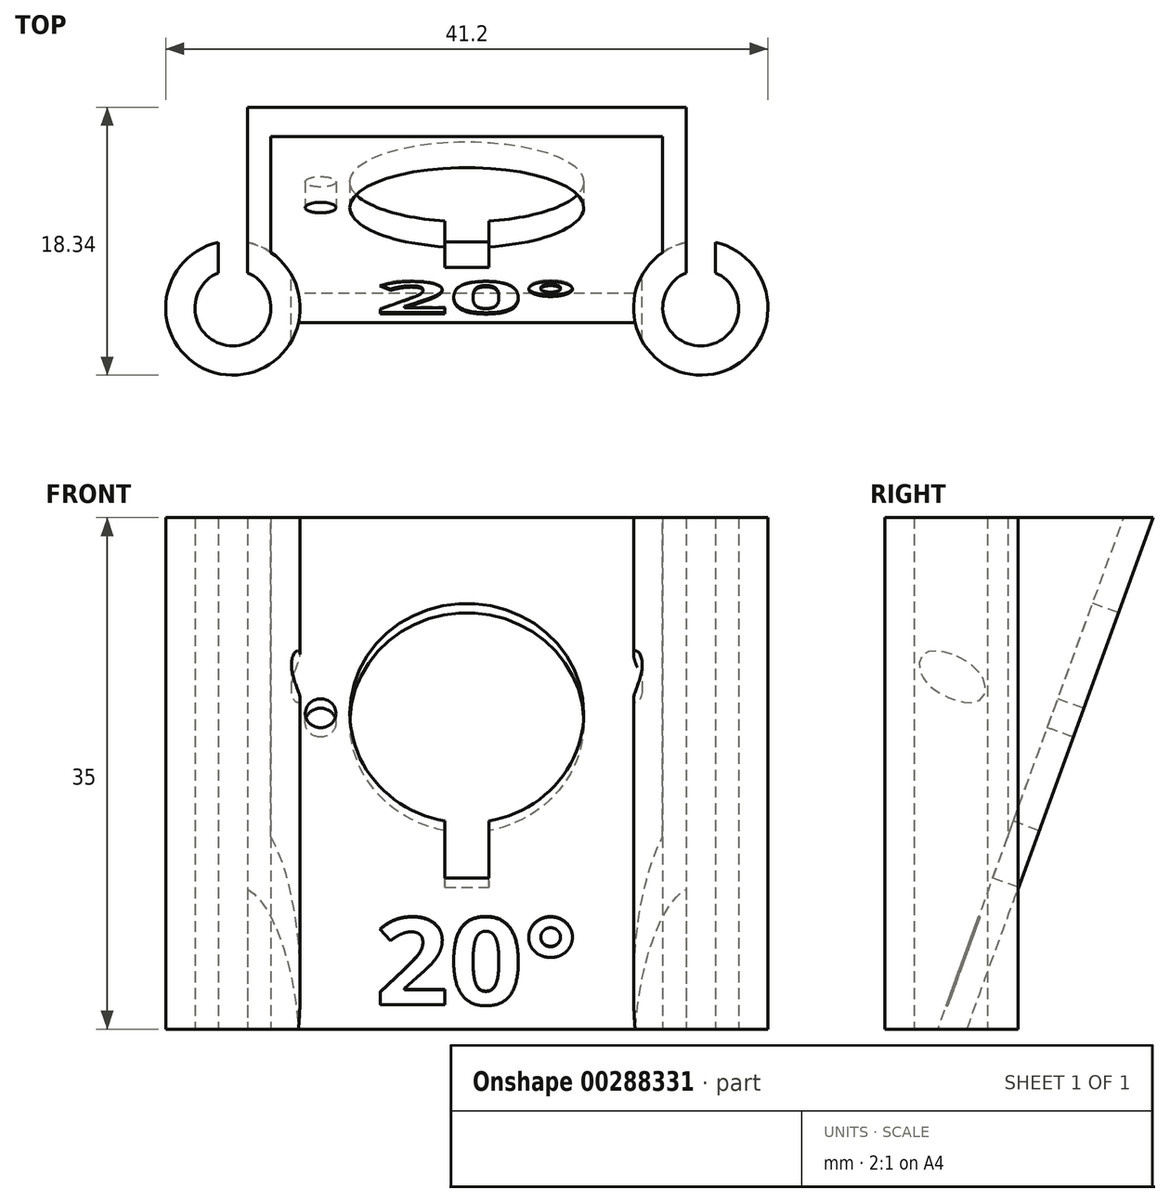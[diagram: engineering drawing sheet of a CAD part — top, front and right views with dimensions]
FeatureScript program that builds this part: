
annotation { "Feature Type Name" : "Feature", "Feature Type Description" : "" }
export const myFeature = defineFeature(function(context is Context, id is Id, definition is map)
    precondition{}
    {
        {
            var Q0;
            Q0=qCreatedBy(makeId("Top.planeOp"),FACE);
            var sketch = newSketch(context, id + "F0", { "sketchPlane" : qUnion([Q0])});
            skLineSegment(sketch, "E0", {"start": v(0, 0) * mm, "end": v(-16, 0) * mm, "construction": true});
            skCircle(sketch, "E1", {"center": v(-16, 0) * mm, "radius": 2.6 * mm});
            skCircle(sketch, "E2.0", {"center": v(-16, 0) * mm, "radius": 4.6 * mm});
            skSolve(sketch);
        }
        {
            var Q0;
            Q0 = qSketchRegion(id + "F0", true);
            extrude(context, id + "F1", {"entities" : qUnion([Q0]), "depth" : 35 * mm});
        }
        {
            var Q0;
            Q0=qCreatedBy(makeId("Top.planeOp"),FACE);
            var sketch = newSketch(context, id + "F2", { "sketchPlane" : qUnion([Q0])});
            skCircle(sketch, "E3.0", {"center": v(-16, 0) * mm, "radius": 2.6 * mm, "construction": true});
            skLineSegment(sketch, "E4", {"start": v(-16, 0) * mm, "end": v(-16, 2.6) * mm, "construction": true});
            skLineSegment(sketch, "E5.bottom", {"start": v(-15, 5.66) * mm, "end": v(-17, 5.66) * mm});
            skLineSegment(sketch, "E5.top", {"start": v(-15, -0.46) * mm, "end": v(-17, -0.46) * mm});
            skLineSegment(sketch, "E5.left", {"start": v(-15, 5.66) * mm, "end": v(-15, -0.46) * mm});
            skLineSegment(sketch, "E5.right", {"start": v(-17, 5.66) * mm, "end": v(-17, -0.46) * mm});
            skPoint(sketch, "E5.middle", {"position": v(-16, 2.6) * mm});
            skSolve(sketch);
        }
        {
            var Q0;
            Q0 = qSketchRegion(id + "F2", true);
            extrude(context, id + "F3", {"entities" : qUnion([Q0]), "operationType" : NewBodyOperationType.REMOVE, "endBound" : BoundingType.THROUGH_ALL, "depth" : 25 * mm});
        }
        {
            var Q0;
            Q0=qCreatedBy(makeId("Top.planeOp"),FACE);
            cPlane(context, id + "F4", {"entities" : qUnion([Q0]), "cplaneType" : CPlaneType.OFFSET, "offset" : 35 * mm, "width" : 150 * mm, "height" : 150 * mm});
        }
        {
            var Q0;
            Q0=makeQuery(id+"F1.opExtrude","SWEPT_BODY",BODY,{"disambiguationData":[OSD([sQuery(id+"F0.wireOp",EDGE,"E1"),sQuery(id+"F0.wireOp",EDGE,"E2.0")])]});
            var Q1;
            Q1=qCreatedBy(makeId("Right.planeOp"),FACE);
            mirror(context, id + "F5", {"entities" : qUnion([Q0]), "mirrorPlane" : qUnion([Q1])});
        }
        {
            var Q0;
            Q0=qCreatedBy(makeId("Top.planeOp"),FACE);
            var sketch = newSketch(context, id + "F6", { "sketchPlane" : qUnion([Q0])});
            skLineSegment(sketch, "E6.bottom", {"start": v(13.4, -1) * mm, "end": v(-13.4, -1) * mm});
            skLineSegment(sketch, "E6.top", {"start": v(13.4, 1) * mm, "end": v(-13.4, 1) * mm});
            skLineSegment(sketch, "E6.left", {"start": v(13.4, -1) * mm, "end": v(13.4, 1) * mm});
            skLineSegment(sketch, "E6.right", {"start": v(-13.4, -1) * mm, "end": v(-13.4, 1) * mm});
            skPoint(sketch, "E6.middle", {"position": v(0, 0) * mm});
            skSolve(sketch);
        }
        {
            var Q0;
            Q0=qCreatedBy(makeId("Right.planeOp"),FACE);
            var sketch = newSketch(context, id + "F7", { "sketchPlane" : qUnion([Q0])});
            skLineSegment(sketch, "E7", {"start": v(0, 0) * mm, "end": v(12.74, 35) * mm, "construction": true});
            skLineSegment(sketch, "E8", {"start": v(12.74, 35) * mm, "end": v(12.74, 0) * mm, "construction": true});
            skLineSegment(sketch, "E9", {"start": v(12.74, 0) * mm, "end": v(0, 0) * mm, "construction": true});
            skSolve(sketch);
        }
        {
            var Q0;
            Q0=qCreatedBy(id+"F4.planeOp",FACE);
            var sketch = newSketch(context, id + "F8", { "sketchPlane" : qUnion([Q0])});
            skLineSegment(sketch, "E10.bottom", {"start": v(13.4, 11.74) * mm, "end": v(-13.4, 11.74) * mm});
            skLineSegment(sketch, "E10.top", {"start": v(13.4, 13.74) * mm, "end": v(-13.4, 13.74) * mm});
            skLineSegment(sketch, "E10.left", {"start": v(13.4, 11.74) * mm, "end": v(13.4, 13.74) * mm});
            skLineSegment(sketch, "E10.right", {"start": v(-13.4, 11.74) * mm, "end": v(-13.4, 13.74) * mm});
            skPoint(sketch, "E10.middle", {"position": v(0, 12.74) * mm});
            skSolve(sketch);
        }
        {
            var Q0;
            Q0 = qSketchRegion(id + "F6", true);
            var Q1;
            Q1 = qSketchRegion(id + "F8", true);
            loft(context, id + "F9", {"operationType" : NewBodyOperationType.ADD, "sheetProfilesArray" : [{ "sheetProfileEntities" : qUnion([Q0]) }, { "sheetProfileEntities" : qUnion([Q1]) }]});
        }
        {
            var Q0;
            Q0=makeQuery(id+"F9.opLoft","SWEPT_FACE",FACE,{"disambiguationData":[OSD([sQuery(id+"F6.wireOp",EDGE,"E6.bottom"),sQuery(id+"F6.wireOp",EDGE,"E6.top"),sQuery(id+"F6.wireOp",EDGE,"E6.left"),sQuery(id+"F8.wireOp",EDGE,"E10.bottom"),sQuery(id+"F8.wireOp",EDGE,"E10.top"),sQuery(id+"F8.wireOp",EDGE,"E10.left")])]});
            var sketch = newSketch(context, id + "F10", { "sketchPlane" : qUnion([Q0])});
            skLineSegment(sketch, "E11", {"start": v(3.8, 35) * mm, "end": v(13.74, 35) * mm});
            skLineSegment(sketch, "E12", {"start": v(3.8, 35) * mm, "end": v(3.8, 7.68) * mm});
            skLineSegment(sketch, "E13", {"start": v(13.74, 35) * mm, "end": v(3.8, 7.68) * mm});
            skSolve(sketch);
        }
        {
            var Q0;
            Q0 = qSketchRegion(id + "F10", true);
            var Q1;
            Q1=makeQuery(id+"F5.opPattern","COPY",FACE,{"derivedFrom":makeQuery(id+"F3.boolean.opBoolean","COPY",FACE,{"derivedFrom":makeQuery(id+"F3.opExtrude","SWEPT_FACE",FACE,{"disambiguationData":[OSD([sQuery(id+"F2.wireOp",EDGE,"E5.left")])]})}),"instanceName":"1"});
            extrude(context, id + "F11", {"entities" : qUnion([Q0]), "operationType" : NewBodyOperationType.ADD, "endBound" : BoundingType.UP_TO_SURFACE, "endBoundEntityFace" : qUnion([Q1]), "depth" : 2 * mm});
        }
        {
            var Q0;
            Q0=makeQuery(id+"F9.opLoft","SWEPT_FACE",FACE,{"disambiguationData":[OSD([sQuery(id+"F6.wireOp",EDGE,"E6.bottom"),sQuery(id+"F6.wireOp",EDGE,"E6.top"),sQuery(id+"F6.wireOp",EDGE,"E6.right"),sQuery(id+"F8.wireOp",EDGE,"E10.bottom"),sQuery(id+"F8.wireOp",EDGE,"E10.top"),sQuery(id+"F8.wireOp",EDGE,"E10.right")])]});
            var sketch = newSketch(context, id + "F12", { "sketchPlane" : qUnion([Q0])});
            skLineSegment(sketch, "E14", {"start": v(-13.74, 35) * mm, "end": v(-3.8, 35) * mm});
            skPoint(sketch, "E14.endSnap0", {"position": v(-12.74, 35) * mm});
            skLineSegment(sketch, "E15", {"start": v(-13.74, 35) * mm, "end": v(-3.8, 7.68) * mm});
            skLineSegment(sketch, "E16", {"start": v(-3.8, 35) * mm, "end": v(-3.8, 7.68) * mm});
            skPoint(sketch, "E17.orphan", {"position": v(2.27, 35) * mm});
            skSolve(sketch);
        }
        {
            var Q0;
            Q0 = qSketchRegion(id + "F12", true);
            var Q1;
            Q1=makeQuery(id+"F3.boolean.opBoolean","COPY",FACE,{"derivedFrom":makeQuery(id+"F3.opExtrude","SWEPT_FACE",FACE,{"disambiguationData":[OSD([sQuery(id+"F2.wireOp",EDGE,"E5.left")])]})});
            extrude(context, id + "F13", {"entities" : qUnion([Q0]), "operationType" : NewBodyOperationType.ADD, "endBound" : BoundingType.UP_TO_SURFACE, "endBoundEntityFace" : qUnion([Q1]), "depth" : 25 * mm});
        }
        {
            var Q0;
            Q0=makeQuery(id+"F9.opLoft","SWEPT_FACE",FACE,{"disambiguationData":[OSD([sQuery(id+"F6.wireOp",EDGE,"E6.bottom"),sQuery(id+"F6.wireOp",EDGE,"E6.left"),sQuery(id+"F6.wireOp",EDGE,"E6.right"),sQuery(id+"F8.wireOp",EDGE,"E10.bottom"),sQuery(id+"F8.wireOp",EDGE,"E10.left"),sQuery(id+"F8.wireOp",EDGE,"E10.right")])]});
            var sketch = newSketch(context, id + "F14", { "sketchPlane" : qUnion([Q0])});
            skCircle(sketch, "E18", {"center": v(0, 22.66) * mm, "radius": 8 * mm});
            skLineSegment(sketch, "E19", {"start": v(0, -0.34) * mm, "end": v(0, 36.9) * mm, "construction": true});
            skSolve(sketch);
        }
        {
            var Q0;
            Q0 = qSketchRegion(id + "F14", true);
            extrude(context, id + "F15", {"entities" : qUnion([Q0]), "operationType" : NewBodyOperationType.REMOVE, "endBound" : BoundingType.THROUGH_ALL, "oppositeDirection" : true, "depth" : 25 * mm});
        }
        {
            var Q0;
            Q0=makeQuery(id+"F9.opLoft","SWEPT_FACE",FACE,{"disambiguationData":[OSD([sQuery(id+"F6.wireOp",EDGE,"E6.bottom"),sQuery(id+"F6.wireOp",EDGE,"E6.left"),sQuery(id+"F6.wireOp",EDGE,"E6.right"),sQuery(id+"F8.wireOp",EDGE,"E10.bottom"),sQuery(id+"F8.wireOp",EDGE,"E10.left"),sQuery(id+"F8.wireOp",EDGE,"E10.right")])]});
            var sketch = newSketch(context, id + "F16", { "sketchPlane" : qUnion([Q0])});
            skLineSegment(sketch, "E20", {"start": v(0, 22.66) * mm, "end": v(-10, 22.66) * mm, "construction": true});
            skCircle(sketch, "E21", {"center": v(-10, 22.66) * mm, "radius": 1.05 * mm});
            skSolve(sketch);
        }
        {
            var Q0;
            Q0 = qSketchRegion(id + "F16", true);
            extrude(context, id + "F17", {"entities" : qUnion([Q0]), "operationType" : NewBodyOperationType.REMOVE, "endBound" : BoundingType.THROUGH_ALL, "oppositeDirection" : true, "depth" : 25 * mm});
        }
        {
            var Q0;
            Q0=makeQuery(id+"F9.opLoft","SWEPT_FACE",FACE,{"disambiguationData":[OSD([sQuery(id+"F6.wireOp",EDGE,"E6.bottom"),sQuery(id+"F6.wireOp",EDGE,"E6.left"),sQuery(id+"F6.wireOp",EDGE,"E6.right"),sQuery(id+"F8.wireOp",EDGE,"E10.bottom"),sQuery(id+"F8.wireOp",EDGE,"E10.left"),sQuery(id+"F8.wireOp",EDGE,"E10.right")])]});
            var sketch = newSketch(context, id + "F18", { "sketchPlane" : qUnion([Q0])});
            skLineSegment(sketch, "E22.bottom", {"start": v(1.5, 10.66) * mm, "end": v(-1.5, 10.66) * mm});
            skLineSegment(sketch, "E22.top", {"start": v(1.5, 18.66) * mm, "end": v(-1.5, 18.66) * mm});
            skLineSegment(sketch, "E22.left", {"start": v(1.5, 10.66) * mm, "end": v(1.5, 18.66) * mm});
            skLineSegment(sketch, "E22.right", {"start": v(-1.5, 10.66) * mm, "end": v(-1.5, 18.66) * mm});
            skPoint(sketch, "E22.middle", {"position": v(0, 14.66) * mm});
            skSolve(sketch);
        }
        {
            var Q0;
            Q0 = qSketchRegion(id + "F18", true);
            extrude(context, id + "F19", {"entities" : qUnion([Q0]), "operationType" : NewBodyOperationType.REMOVE, "endBound" : BoundingType.THROUGH_ALL, "oppositeDirection" : true, "depth" : 25 * mm});
        }
        {
            var Q0;
            Q0=makeQuery(id+"F9.opLoft","SWEPT_FACE",FACE,{"disambiguationData":[OSD([sQuery(id+"F6.wireOp",EDGE,"E6.bottom"),sQuery(id+"F6.wireOp",EDGE,"E6.left"),sQuery(id+"F6.wireOp",EDGE,"E6.right"),sQuery(id+"F8.wireOp",EDGE,"E10.bottom"),sQuery(id+"F8.wireOp",EDGE,"E10.left"),sQuery(id+"F8.wireOp",EDGE,"E10.right")])]});
            var sketch = newSketch(context, id + "F20", { "sketchPlane" : qUnion([Q0])});
            skCircle(sketch, "E23", {"center": v(-10, 22.66) * mm, "radius": 2 * mm});
            skCircle(sketch, "E24", {"center": v(10, 22.66) * mm, "radius": 2 * mm});
            skSolve(sketch);
        }
        {
            var Q0;
            Q0 = qSketchRegion(id + "F20", true);
            extrude(context, id + "F21", {"entities" : qUnion([Q0]), "operationType" : NewBodyOperationType.REMOVE, "endBound" : BoundingType.THROUGH_ALL, "depth" : 25 * mm});
        }
        {
            var Q0;
            Q0=makeQuery(id+"F9.opLoft","SWEPT_FACE",FACE,{"disambiguationData":[OSD([sQuery(id+"F6.wireOp",EDGE,"E6.bottom"),sQuery(id+"F6.wireOp",EDGE,"E6.left"),sQuery(id+"F6.wireOp",EDGE,"E6.right"),sQuery(id+"F8.wireOp",EDGE,"E10.bottom"),sQuery(id+"F8.wireOp",EDGE,"E10.left"),sQuery(id+"F8.wireOp",EDGE,"E10.right")])]});
            var sketch = newSketch(context, id + "F22", { "sketchPlane" : qUnion([Q0])});
            skText(sketch, "E25", { "text": "20°", "fontName": "OpenSans-Bold.ttf"});
            const initialGuessF22  = {"E25": [-0.00628, 0.00144, 1, 0, 0.00638]};
            skSetInitialGuess(sketch, initialGuessF22);
            skSolve(sketch);
        }
        {
            var Q0;
            Q0 = qSketchRegion(id + "F22", true);
            extrude(context, id + "F23", {"entities" : qUnion([Q0]), "operationType" : NewBodyOperationType.REMOVE, "oppositeDirection" : true, "depth" : 0.1 * mm});
        }
    });
